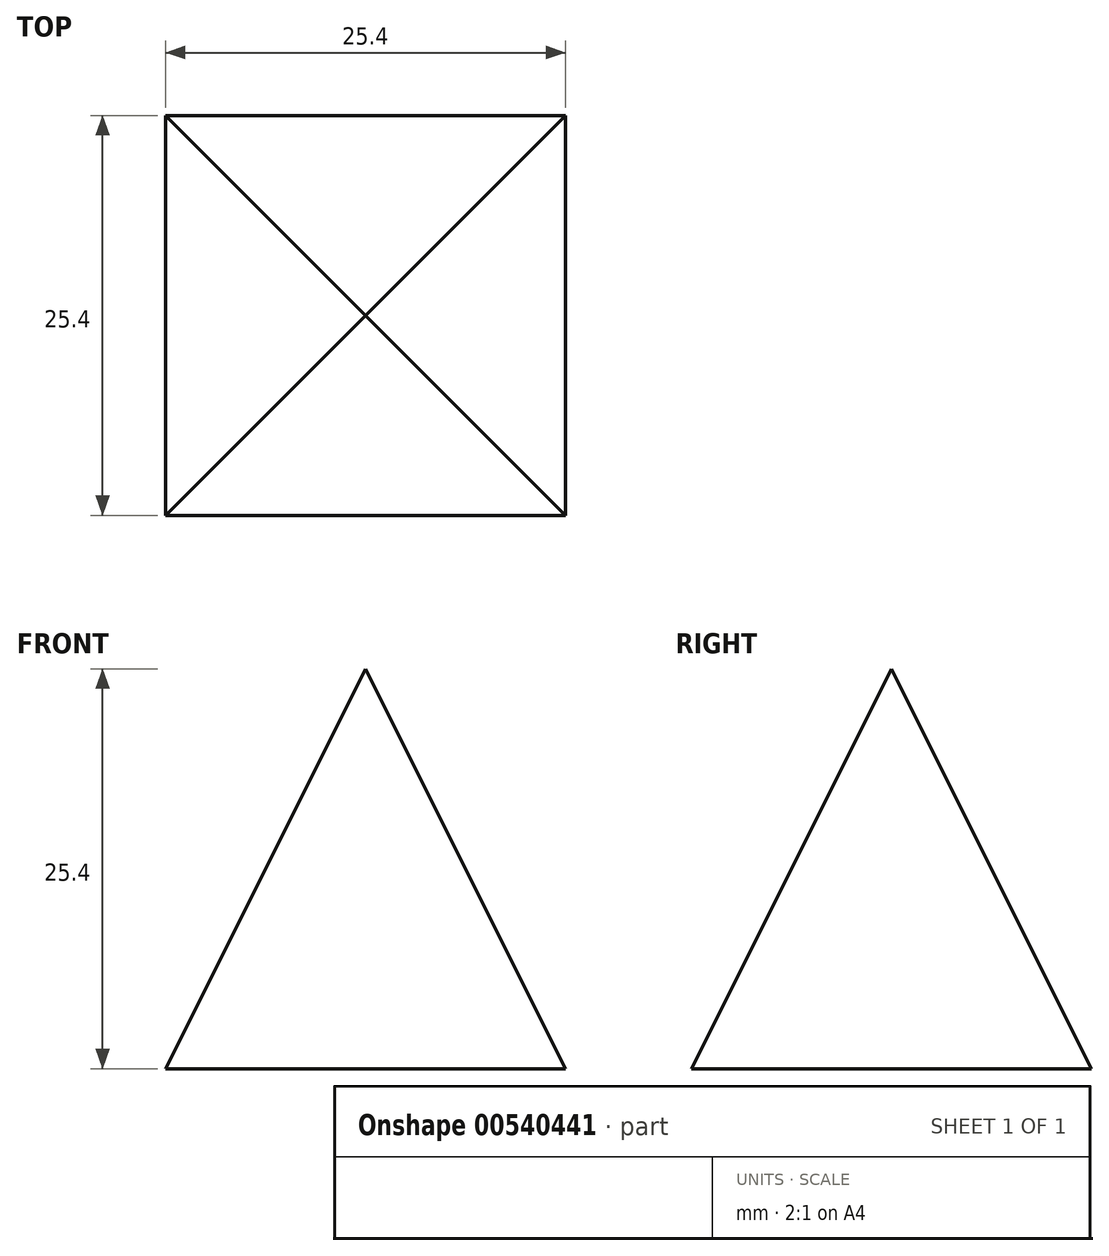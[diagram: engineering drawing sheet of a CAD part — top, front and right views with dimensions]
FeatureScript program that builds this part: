
annotation { "Feature Type Name" : "Feature", "Feature Type Description" : "" }
export const myFeature = defineFeature(function(context is Context, id is Id, definition is map)
    precondition{}
    {
        {
            var Q0;
            Q0=qCreatedBy(makeId("Top.planeOp"),FACE);
            var sketch = newSketch(context, id + "F0", { "sketchPlane" : qUnion([Q0])});
            skLineSegment(sketch, "E0.bottom", {"start": v(12.7, 12.7) * mm, "end": v(-12.7, 12.7) * mm});
            skLineSegment(sketch, "E0.top", {"start": v(12.7, -12.7) * mm, "end": v(-12.7, -12.7) * mm});
            skLineSegment(sketch, "E0.left", {"start": v(12.7, 12.7) * mm, "end": v(12.7, -12.7) * mm});
            skLineSegment(sketch, "E0.right", {"start": v(-12.7, 12.7) * mm, "end": v(-12.7, -12.7) * mm});
            skPoint(sketch, "E0.middle", {"position": v(0, 0) * mm});
            skSolve(sketch);
        }
        {
            var Q0;
            Q0=qCreatedBy(makeId("Top.planeOp"),FACE);
            cPlane(context, id + "F1", {"entities" : qUnion([Q0]), "cplaneType" : CPlaneType.OFFSET, "offset" : 25.4 * mm, "width" : 152.4 * mm, "height" : 152.4 * mm});
        }
        {
            var Q0;
            Q0=qCreatedBy(id+"F1.planeOp",FACE);
            var sketch = newSketch(context, id + "F2", { "sketchPlane" : qUnion([Q0])});
            skPoint(sketch, "E1", {"position": v(0, 0) * mm});
            skSolve(sketch);
        }
        {
            var Q0;
            Q0=makeQuery(id+"F0.imprint","IMPRINT",FACE,{"disambiguationData":[TD([[makeQuery(id+"F0.imprint","IMPRINT",EDGE,{"derivedFrom":sQuery(id+"F0.wireOp",EDGE,"E0.bottom")}),1.0]])]});
            var Q1;
            Q1=sQuery(id+"F2.wireOp",VERTEX,"E1");
            loft(context, id + "F3", {"sheetProfilesArray" : [{ "sheetProfileEntities" : qUnion([Q0]) }, { "sheetProfileEntities" : qUnion([Q1]) }]});
        }
    });
